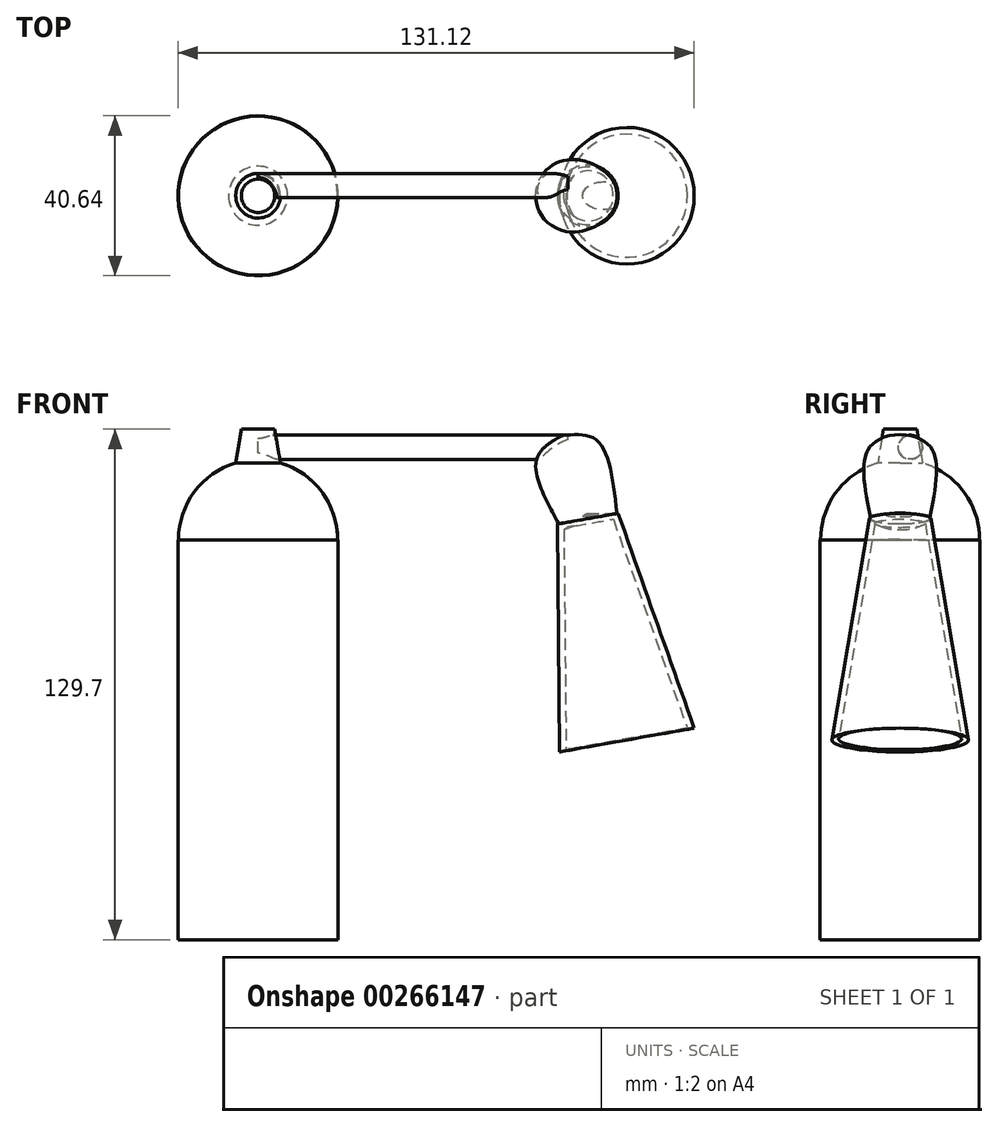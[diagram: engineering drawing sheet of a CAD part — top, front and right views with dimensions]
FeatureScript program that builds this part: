
annotation { "Feature Type Name" : "Feature", "Feature Type Description" : "" }
export const myFeature = defineFeature(function(context is Context, id is Id, definition is map)
    precondition{}
    {
        {
            var Q0;
            Q0=qCreatedBy(makeId("Top.planeOp"),FACE);
            var sketch = newSketch(context, id + "F0", { "sketchPlane" : qUnion([Q0])});
            skCircle(sketch, "E0", {"center": v(0, 0) * mm, "radius": 20.32 * mm});
            skSolve(sketch);
        }
        {
            var Q0;
            Q0 = qSketchRegion(id + "F0", true);
            extrude(context, id + "F1", {"entities" : qUnion([Q0]), "endBound" : BoundingType.SYMMETRIC, "depth" : 101.6 * mm});
        }
        {
            var Q0;
            Q0=qCreatedBy(makeId("Front.planeOp"),FACE);
            var sketch = newSketch(context, id + "F2", { "sketchPlane" : qUnion([Q0])});
            skArc(sketch, "E1", {"start": v(20.19, 50.58) * mm, "mid": v(14.4, 65.08) * mm, "end": v(0, 71.12) * mm});
            skLineSegment(sketch, "E2", {"start": v(0, 71.12) * mm, "end": v(0, 50.93) * mm});
            skLineSegment(sketch, "E3", {"start": v(0, 50.93) * mm, "end": v(20.19, 50.58) * mm});
            skSolve(sketch);
        }
        {
            var Q0;
            Q0 = qSketchRegion(id + "F2", true);
            var Q1;
            Q1=sQuery(id+"F2.wireOp",EDGE,"E2");
            revolve(context, id + "F3", {"operationType" : NewBodyOperationType.ADD, "entities" : qUnion([Q0]), "axis" : qUnion([Q1]), "revolveType" : RevolveType.FULL});
        }
        {
            var Q0;
            Q0=makeQuery(id+"F1.opExtrude","CAP_FACE",FACE,{"disambiguationData":[OSD([sQuery(id+"F0.wireOp",EDGE,"E0")])],"isStart":true});
            cPlane(context, id + "F4", {"entities" : qUnion([Q0]), "cplaneType" : CPlaneType.OFFSET, "offset" : 101.6 * mm, "oppositeDirection" : true, "width" : 152.4 * mm, "height" : 152.4 * mm});
        }
        {
            var Q0;
            Q0=qCreatedBy(makeId("Right.planeOp"),FACE);
            var sketch = newSketch(context, id + "F5", { "sketchPlane" : qUnion([Q0])});
            skLineSegment(sketch, "E4", {"start": v(1.66, 62.31) * mm, "end": v(7, 62.31) * mm});
            skLineSegment(sketch, "E5", {"start": v(7, 62.31) * mm, "end": v(4.24, 78.9) * mm});
            skLineSegment(sketch, "E6", {"start": v(4.24, 78.9) * mm, "end": v(0, 78.9) * mm});
            skLineSegment(sketch, "E7", {"start": v(0, 78.9) * mm, "end": v(0, 62.31) * mm});
            skLineSegment(sketch, "E8", {"start": v(0, 62.31) * mm, "end": v(1.66, 62.31) * mm});
            skSolve(sketch);
        }
        {
            var Q0;
            Q0 = qSketchRegion(id + "F5", true);
            var Q1;
            Q1=sQuery(id+"F5.wireOp",EDGE,"E7");
            revolve(context, id + "F6", {"operationType" : NewBodyOperationType.ADD, "entities" : qUnion([Q0]), "axis" : qUnion([Q1]), "revolveType" : RevolveType.FULL});
        }
        {
            var Q0;
            Q0=qCreatedBy(makeId("Right.planeOp"),FACE);
            var sketch = newSketch(context, id + "F7", { "sketchPlane" : qUnion([Q0])});
            skCircle(sketch, "E9", {"center": v(2.58, 74.31) * mm, "radius": 3.07 * mm});
            skSolve(sketch);
        }
        {
            var Q0;
            Q0 = qSketchRegion(id + "F7", true);
            extrude(context, id + "F8", {"entities" : qUnion([Q0]), "operationType" : NewBodyOperationType.ADD, "depth" : 78.74 * mm});
        }
        {
            var Q0;
            Q0=qCreatedBy(makeId("Front.planeOp"),FACE);
            var sketch = newSketch(context, id + "F9", { "sketchPlane" : qUnion([Q0])});
            skFitSpline(sketch, "E10", {"points": [v(77.2, 77.27) * mm, v(86.13, 76.01) * mm, v(91.19, 57.6) * mm], "startDerivative": vector(24.67, 2.61) * mm, "endDerivative": vector(4.57, -39.36) * mm});
            skFitSpline(sketch, "E11", {"points": [v(79.2, 74.62) * mm, v(83.63, 73.47) * mm, v(83.59, 57.47) * mm], "startDerivative": vector(14.95, 0.4) * mm, "endDerivative": vector(-4.23, -31.48) * mm});
            skLineSegment(sketch, "E12", {"start": v(77.2, 77.27) * mm, "end": v(79.2, 74.62) * mm});
            skLineSegment(sketch, "E13", {"start": v(83.59, 57.47) * mm, "end": v(91.19, 57.6) * mm});
            skLineSegment(sketch, "E14", {"start": v(77.2, 77.27) * mm, "end": v(83.59, 57.47) * mm});
            skSolve(sketch);
        }
        {
            var Q0;
            Q0 = qSketchRegion(id + "F9", true);
            var Q1;
            Q1=sQuery(id+"F9.wireOp",EDGE,"E14");
            revolve(context, id + "F10", {"operationType" : NewBodyOperationType.ADD, "entities" : qUnion([Q0]), "axis" : qUnion([Q1]), "revolveType" : RevolveType.FULL});
        }
        {
            var Q0;
            Q0=qCreatedBy(makeId("Front.planeOp"),FACE);
            var sketch = newSketch(context, id + "F11", { "sketchPlane" : qUnion([Q0])});
            skLineSegment(sketch, "E15", {"start": v(83.6, 57.01) * mm, "end": v(93.16, 2.95) * mm});
            skLineSegment(sketch, "E16", {"start": v(93.16, 2.95) * mm, "end": v(110.8, 2.95) * mm});
            skLineSegment(sketch, "E17", {"start": v(110.8, 2.95) * mm, "end": v(91.47, 57.52) * mm});
            skLineSegment(sketch, "E18", {"start": v(83.6, 57.01) * mm, "end": v(91.47, 57.52) * mm});
            skLineSegment(sketch, "E19", {"start": v(109.04, 2.95) * mm, "end": v(90.23, 56.06) * mm});
            skLineSegment(sketch, "E20", {"start": v(90.23, 56.06) * mm, "end": v(83.97, 54.95) * mm});
            skSolve(sketch);
        }
        {
            var Q0;
            {var subQ1=sQuery(id+"F11.wireOp",EDGE,"E17");Q0=makeQuery(id+"F11.imprint","IMPRINT",FACE,{"disambiguationData":[TD([[makeQuery(id+"F11.imprint","IMPRINT",EDGE,{"derivedFrom":subQ1}),1.0]])]});}
            var Q1;
            Q1=sQuery(id+"F11.wireOp",EDGE,"E15");
            revolve(context, id + "F12", {"operationType" : NewBodyOperationType.ADD, "entities" : qUnion([Q0]), "axis" : qUnion([Q1]), "revolveType" : RevolveType.FULL});
        }
    });
